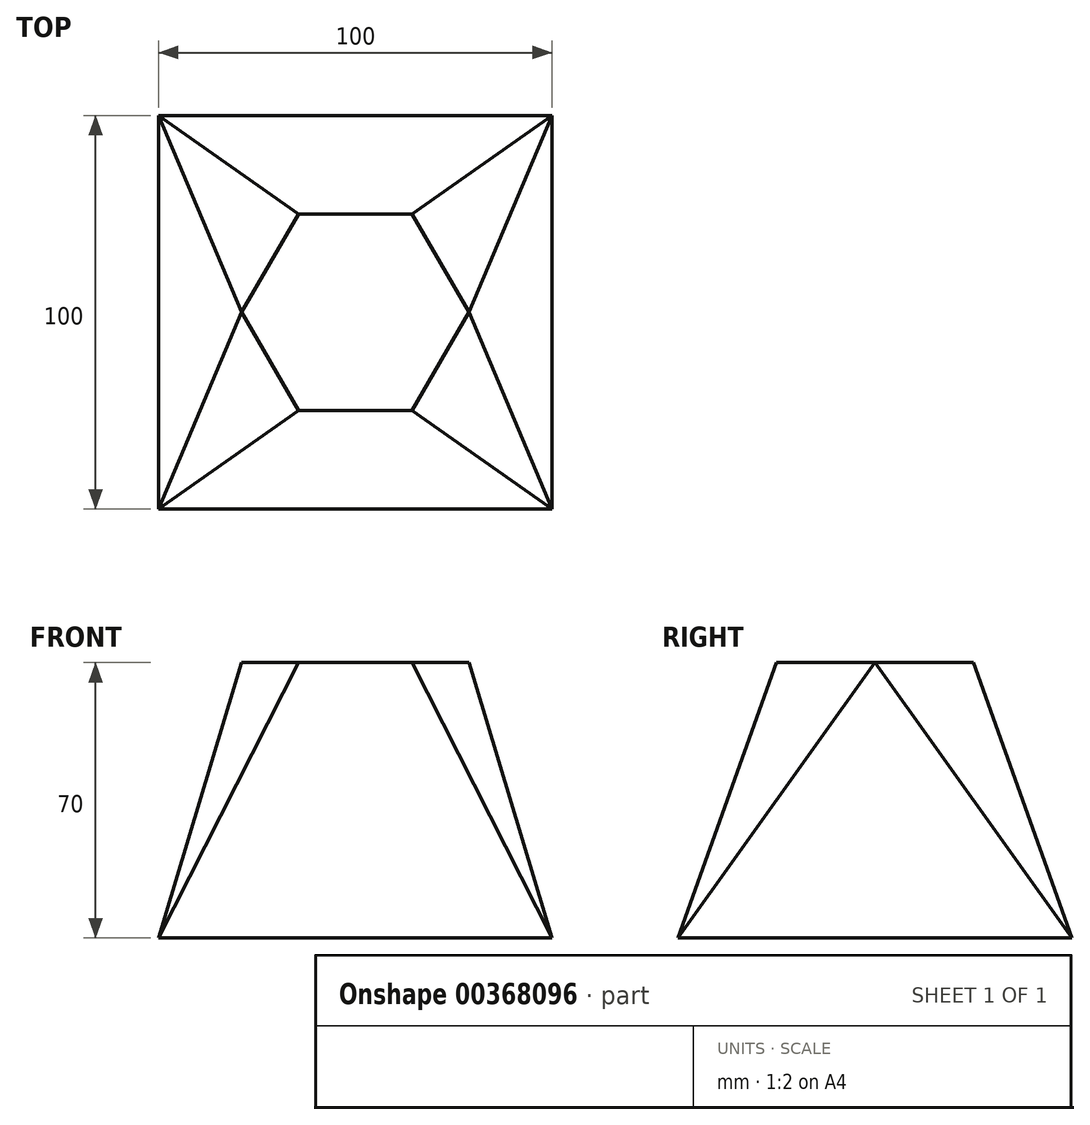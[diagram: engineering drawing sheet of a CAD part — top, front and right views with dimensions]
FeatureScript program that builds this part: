
annotation { "Feature Type Name" : "Feature", "Feature Type Description" : "" }
export const myFeature = defineFeature(function(context is Context, id is Id, definition is map)
    precondition{}
    {
        {
            var Q0;
            Q0=qCreatedBy(makeId("Top.planeOp"),FACE);
            var sketch = newSketch(context, id + "F0", { "sketchPlane" : qUnion([Q0])});
            skLineSegment(sketch, "E0.bottom", {"start": v(50, -50) * mm, "end": v(-50, -50) * mm});
            skLineSegment(sketch, "E0.top", {"start": v(50, 50) * mm, "end": v(-50, 50) * mm});
            skLineSegment(sketch, "E0.left", {"start": v(50, -50) * mm, "end": v(50, 50) * mm});
            skLineSegment(sketch, "E0.right", {"start": v(-50, -50) * mm, "end": v(-50, 50) * mm});
            skPoint(sketch, "E0.middle", {"position": v(0, 0) * mm});
            skSolve(sketch);
        }
        {
            var Q0;
            Q0=qCreatedBy(makeId("Top.planeOp"),FACE);
            cPlane(context, id + "F1", {"entities" : qUnion([Q0]), "cplaneType" : CPlaneType.OFFSET, "offset" : 70 * mm, "width" : 150 * mm, "height" : 150 * mm});
        }
        {
            var Q0;
            Q0=qCreatedBy(id+"F1.planeOp",FACE);
            var sketch = newSketch(context, id + "F2", { "sketchPlane" : qUnion([Q0])});
            skCircle(sketch, "E1.cCircle", {"center": v(0, 0) * mm, "radius": 28.87 * mm, "construction": true});
            skLineSegment(sketch, "E1.0", {"start": v(28.87, 0) * mm, "end": v(14.43, -25) * mm});
            skLineSegment(sketch, "E1.1", {"start": v(14.43, -25) * mm, "end": v(-14.43, -25) * mm});
            skLineSegment(sketch, "E1.2", {"start": v(-14.43, -25) * mm, "end": v(-28.87, 0) * mm});
            skLineSegment(sketch, "E1.3", {"start": v(-28.87, 0) * mm, "end": v(-14.43, 25) * mm});
            skLineSegment(sketch, "E1.4", {"start": v(-14.43, 25) * mm, "end": v(14.43, 25) * mm});
            skLineSegment(sketch, "E1.5", {"start": v(14.43, 25) * mm, "end": v(28.87, 0) * mm});
            skLineSegment(sketch, "E2.bottom", {"start": v(28.87, -25) * mm, "end": v(-28.87, -25) * mm});
            skLineSegment(sketch, "E2.top", {"start": v(28.87, 25) * mm, "end": v(-28.87, 25) * mm});
            skLineSegment(sketch, "E2.left", {"start": v(28.87, -25) * mm, "end": v(28.87, 25) * mm});
            skLineSegment(sketch, "E2.right", {"start": v(-28.87, -25) * mm, "end": v(-28.87, 25) * mm});
            skSolve(sketch);
        }
        {
            var Q0;
            Q0=qCreatedBy(id+"F1.planeOp",FACE);
            var sketch = newSketch(context, id + "F3", { "sketchPlane" : qUnion([Q0])});
            skLineSegment(sketch, "E3.bottom", {"start": v(28.87, -25) * mm, "end": v(-28.87, -25) * mm});
            skLineSegment(sketch, "E3.top", {"start": v(28.87, 25) * mm, "end": v(-28.87, 25) * mm});
            skLineSegment(sketch, "E3.left", {"start": v(28.87, -25) * mm, "end": v(28.87, 25) * mm});
            skLineSegment(sketch, "E3.right", {"start": v(-28.87, -25) * mm, "end": v(-28.87, 25) * mm});
            skPoint(sketch, "E3.middle", {"position": v(0, 0) * mm});
            skSolve(sketch);
        }
        {
            var Q0;
            Q0=makeQuery(id+"F3.imprint","IMPRINT",FACE,{"disambiguationData":[TD([[makeQuery(id+"F3.imprint","IMPRINT",EDGE,{"derivedFrom":sQuery(id+"F3.wireOp",EDGE,"E3.bottom")}),-1.0]])]});
            var Q1;
            Q1=makeQuery(id+"F0.imprint","IMPRINT",FACE,{"disambiguationData":[TD([[makeQuery(id+"F0.imprint","IMPRINT",EDGE,{"derivedFrom":sQuery(id+"F0.wireOp",EDGE,"E0.bottom")}),-1.0]])]});
            loft(context, id + "F4", {"sheetProfilesArray" : [{ "sheetProfileEntities" : qUnion([Q0]) }, { "sheetProfileEntities" : qUnion([Q1]) }]});
        }
        {
            var Q1;
            {var subQ0=sQuery(id+"F2.wireOp",EDGE,"E1.3");Q1=makeQuery(id+"F2.imprint","IMPRINT",FACE,{"disambiguationData":[TD([[makeQuery(id+"F2.imprint","IMPRINT",EDGE,{"derivedFrom":subQ0}),1.0]])]});}
            var Q2;
            Q2=sQuery(id+"F0.wireOp",VERTEX,"E0.right.end");
            loft(context, id + "F5", {"operationType" : NewBodyOperationType.REMOVE, "sheetProfilesArray" : [{ "sheetProfileEntities" : qUnion([Q1]) }, { "sheetProfileEntities" : qUnion([Q2]) }]});
        }
        {
            var Q1;
            {var subQ0=sQuery(id+"F2.wireOp",EDGE,"E1.2");Q1=makeQuery(id+"F2.imprint","IMPRINT",FACE,{"disambiguationData":[TD([[makeQuery(id+"F2.imprint","IMPRINT",EDGE,{"derivedFrom":subQ0}),1.0]])]});}
            var Q2;
            Q2=sQuery(id+"F0.wireOp",VERTEX,"E0.right.start");
            loft(context, id + "F6", {"operationType" : NewBodyOperationType.REMOVE, "sheetProfilesArray" : [{ "sheetProfileEntities" : qUnion([Q1]) }, { "sheetProfileEntities" : qUnion([Q2]) }]});
        }
        {
            var Q1;
            {var subQ0=sQuery(id+"F2.wireOp",EDGE,"E1.0");Q1=makeQuery(id+"F2.imprint","IMPRINT",FACE,{"disambiguationData":[TD([[makeQuery(id+"F2.imprint","IMPRINT",EDGE,{"derivedFrom":subQ0}),1.0]])]});}
            var Q2;
            Q2=sQuery(id+"F0.wireOp",VERTEX,"E0.left.start");
            loft(context, id + "F7", {"operationType" : NewBodyOperationType.REMOVE, "sheetProfilesArray" : [{ "sheetProfileEntities" : qUnion([Q1]) }, { "sheetProfileEntities" : qUnion([Q2]) }]});
        }
        {
            var Q1;
            {var subQ0=sQuery(id+"F2.wireOp",EDGE,"E1.5");Q1=makeQuery(id+"F2.imprint","IMPRINT",FACE,{"disambiguationData":[TD([[makeQuery(id+"F2.imprint","IMPRINT",EDGE,{"derivedFrom":subQ0}),1.0]])]});}
            var Q2;
            Q2=sQuery(id+"F0.wireOp",VERTEX,"E0.top.start");
            loft(context, id + "F8", {"operationType" : NewBodyOperationType.REMOVE, "sheetProfilesArray" : [{ "sheetProfileEntities" : qUnion([Q1]) }, { "sheetProfileEntities" : qUnion([Q2]) }]});
        }
    });
